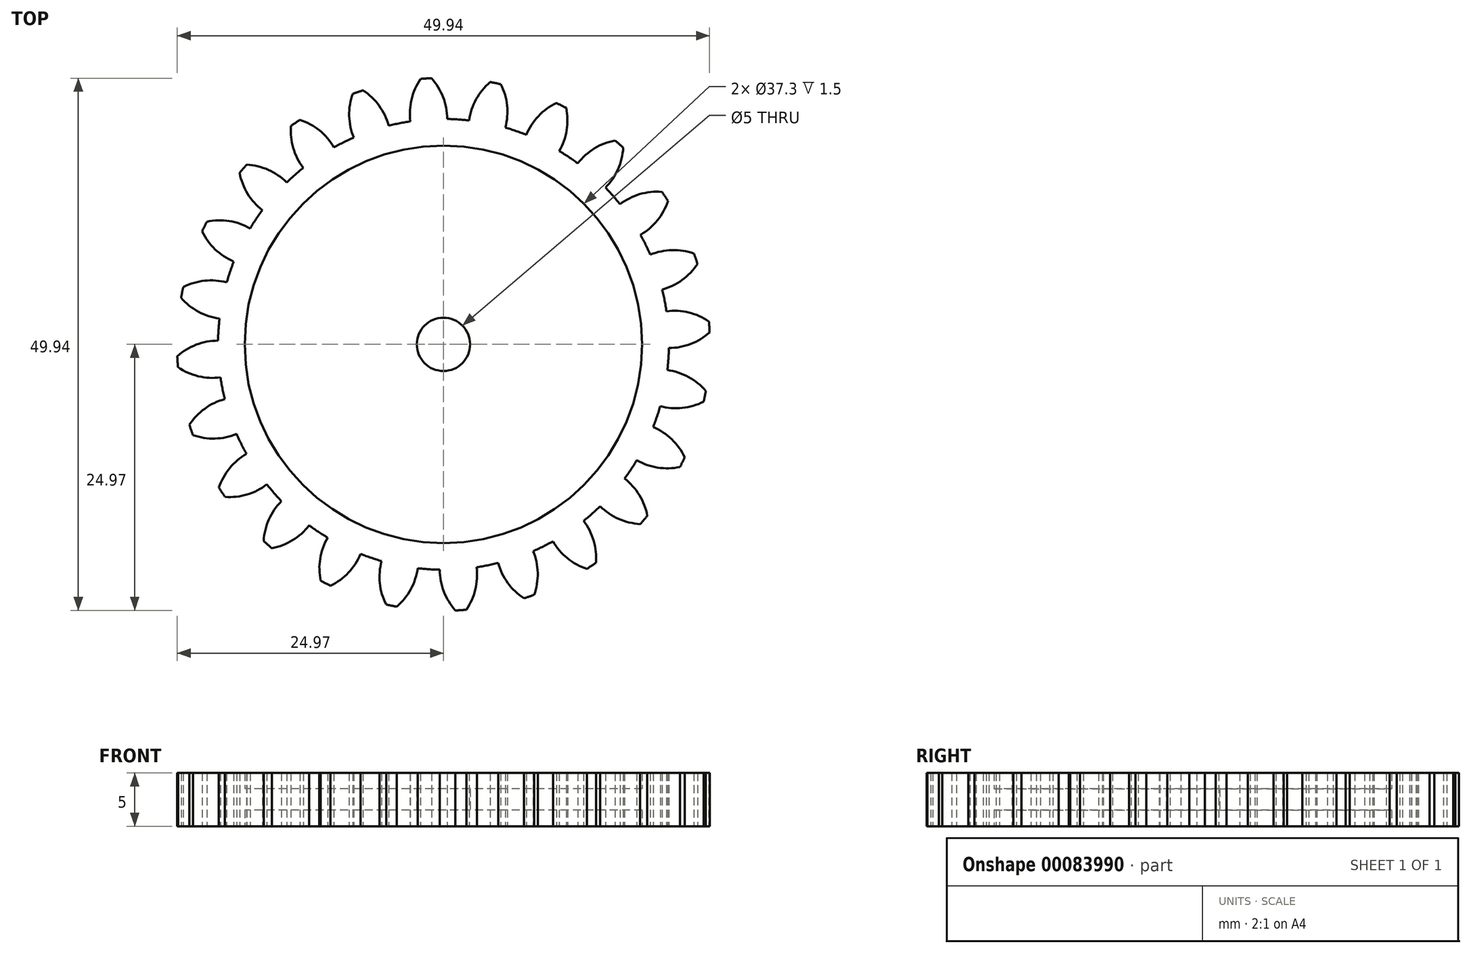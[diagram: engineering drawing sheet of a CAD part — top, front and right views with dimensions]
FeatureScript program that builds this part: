
annotation { "Feature Type Name" : "Feature", "Feature Type Description" : "" }
export const myFeature = defineFeature(function(context is Context, id is Id, definition is map)
    precondition{}
    {
        {
            var Q0;
            Q0=qCreatedBy(makeId("Top.planeOp"),FACE);
            var sketch = newSketch(context, id + "F0", { "sketchPlane" : qUnion([Q0])});
            skCircle(sketch, "E0", {"center": v(0, 0) * mm, "radius": 21.15 * mm});
            skCircle(sketch, "E1", {"center": v(0, 0) * mm, "radius": 23.1 * mm, "construction": true});
            skCircle(sketch, "E2", {"center": v(0, 0) * mm, "radius": 25 * mm, "construction": true});
            skLineSegment(sketch, "E3", {"start": v(0, 0) * mm, "end": v(0, 39.12) * mm, "construction": true});
            skLineSegment(sketch, "E4", {"start": v(0, 0) * mm, "end": v(-2.56, 38.99) * mm, "construction": true});
            skLineSegment(sketch, "E5", {"start": v(0, 23.1) * mm, "end": v(-34.67, 23.1) * mm, "construction": true});
            skLineSegment(sketch, "E6", {"start": v(0, 23.1) * mm, "end": v(-33.2, 11.02) * mm, "construction": true});
            skCircle(sketch, "E7", {"center": v(0, 23.1) * mm, "radius": 5.75 * mm, "construction": true});
            skCircle(sketch, "E8", {"center": v(-5.4, 21.13) * mm, "radius": 5.75 * mm, "construction": true});
            skArc(sketch, "E9", {"start": v(0.35, 21.15) * mm, "mid": v(-0.04, 23.2) * mm, "end": v(-1.12, 24.97) * mm});
            skArc(sketch, "E10.MirrorCS", {"start": v(-3.1, 20.92) * mm, "mid": v(-3, 23) * mm, "end": v(-2.14, 24.9) * mm});
            skArc(sketch, "E11", {"start": v(-1.12, 24.97) * mm, "mid": v(-1.64, 24.95) * mm, "end": v(-2.14, 24.9) * mm});
            skCircle(sketch, "E12", {"center": v(0, 0) * mm, "radius": 2.5 * mm});
            skCircle(sketch, "E13", {"center": v(0, 0) * mm, "radius": 18.65 * mm});
            skSolve(sketch);
        }
        {
            var Q0;
            {var subQ0=sQuery(id+"F0.wireOp",EDGE,"E9");Q0=makeQuery(id+"F0.imprint","IMPRINT",FACE,{"disambiguationData":[TD([[makeQuery(id+"F0.imprint","IMPRINT",EDGE,{"derivedFrom":subQ0}),1.0]])]});}
            var Q1;
            {var subQ0=sQuery(id+"F0.wireOp",EDGE,"E0");var subQ1=makeQuery(id+"F0.imprint","INTERSECT",VERTEX,{"derivedFrom":[subQ0,sQuery(id+"F0.wireOp",EDGE,"E9")]});Q1=makeQuery(id+"F0.imprint","IMPRINT",FACE,{"disambiguationData":[TD([[makeQuery(id+"F0.imprint","IMPRINT",EDGE,{"disambiguationData":[TD([[subQ1,-1.0]])],"derivedFrom":subQ0}),1.0]])]});}
            extrude(context, id + "F1", {"entities" : qUnion([Q0, Q1]), "depth" : 5 * mm});
        }
        {
            var Q0;
            Q0=qCreatedBy(makeId("Front.planeOp"),FACE);
            var sketch = newSketch(context, id + "F2", { "sketchPlane" : qUnion([Q0])});
            skLineSegment(sketch, "E14", {"start": v(0, 0) * mm, "end": v(0, 28.22) * mm, "construction": true});
            skSolve(sketch);
        }
        {
            var Q0;
            Q0=makeQuery(id+"F1.opExtrude","SWEPT_BODY",BODY,{"disambiguationData":[OSD([sQuery(id+"F0.wireOp",EDGE,"E0"),sQuery(id+"F0.wireOp",EDGE,"E9"),sQuery(id+"F0.wireOp",EDGE,"E10.MirrorCS"),sQuery(id+"F0.wireOp",EDGE,"E11")])]});
            var Q1;
            Q1=sQuery(id+"F2.wireOp",EDGE,"E14");
            circularPattern(context, id + "F3", {"operationType" : NewBodyOperationType.ADD, "entities" : qUnion([Q0]), "axis" : qUnion([Q1]), "angle" : 15 * degree, "instanceCount" : 24});
        }
        {
            var Q0;
            Q0=makeQuery(id+"F0.imprint","IMPRINT",FACE,{"disambiguationData":[TD([[makeQuery(id+"F0.imprint","IMPRINT",EDGE,{"derivedFrom":sQuery(id+"F0.wireOp",EDGE,"E12")}),-1.0]])]});
            extrude(context, id + "F4", {"entities" : qUnion([Q0]), "operationType" : NewBodyOperationType.ADD, "depth" : 3.5 * mm, "hasSecondDirection" : true, "secondDirectionOppositeDirection" : false, "secondDirectionDepth" : 1.5 * mm});
        }
    });
